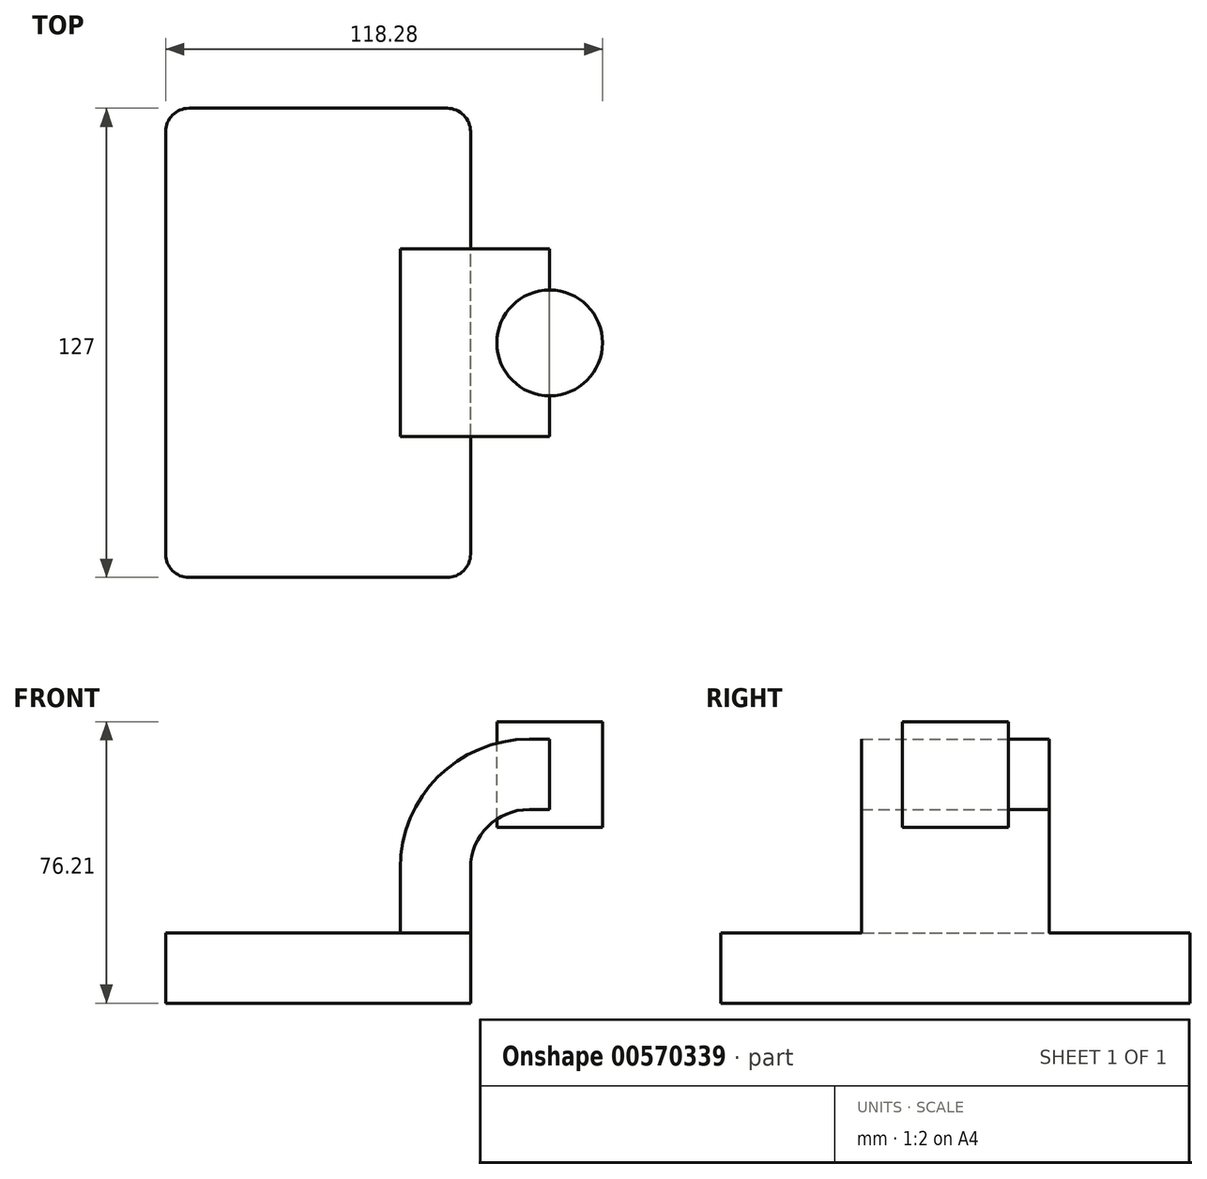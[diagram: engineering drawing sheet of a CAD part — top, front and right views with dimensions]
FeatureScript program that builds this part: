
annotation { "Feature Type Name" : "Feature", "Feature Type Description" : "" }
export const myFeature = defineFeature(function(context is Context, id is Id, definition is map)
    precondition{}
    {
        {
            var Q0;
            Q0=qCreatedBy(makeId("Front.planeOp"),FACE);
            var sketch = newSketch(context, id + "F0", { "sketchPlane" : qUnion([Q0])});
            skLineSegment(sketch, "E0.bottom", {"start": v(-41.28, 9.52) * mm, "end": v(41.27, 9.53) * mm});
            skLineSegment(sketch, "E0.top", {"start": v(-41.28, -9.53) * mm, "end": v(41.28, -9.53) * mm});
            skLineSegment(sketch, "E0.left", {"start": v(-41.28, 9.52) * mm, "end": v(-41.28, -9.53) * mm});
            skLineSegment(sketch, "E0.right", {"start": v(41.27, 9.53) * mm, "end": v(41.28, -9.52) * mm});
            skPoint(sketch, "E0.middle", {"position": v(0, 0) * mm});
            skLineSegment(sketch, "E1.bottom", {"start": v(62.7, 66.67) * mm, "end": v(113.5, 66.67) * mm});
            skLineSegment(sketch, "E1.top", {"start": v(62.7, 38.1) * mm, "end": v(113.5, 38.1) * mm});
            skLineSegment(sketch, "E1.left", {"start": v(62.7, 66.67) * mm, "end": v(62.7, 38.1) * mm});
            skLineSegment(sketch, "E1.right", {"start": v(113.5, 66.67) * mm, "end": v(113.5, 38.1) * mm});
            skPoint(sketch, "E1.middle", {"position": v(88.1, 52.39) * mm});
            skLineSegment(sketch, "E2", {"start": v(41.27, 9.53) * mm, "end": v(41.27, 27) * mm});
            skArc(sketch, "E3", {"start": v(41.27, 27) * mm, "mid": v(45.92, 38.23) * mm, "end": v(57.15, 42.88) * mm});
            skLineSegment(sketch, "E4", {"start": v(57.15, 42.88) * mm, "end": v(77, 42.88) * mm});
            skLineSegment(sketch, "E5.0", {"start": v(57.15, 61.93) * mm, "end": v(77, 61.93) * mm});
            skArc(sketch, "E5.1", {"start": v(22.22, 27) * mm, "mid": v(32.45, 51.7) * mm, "end": v(57.15, 61.93) * mm});
            skLineSegment(sketch, "E5.2", {"start": v(22.22, 9.53) * mm, "end": v(22.22, 27) * mm});
            skLineSegment(sketch, "E6", {"start": v(77.01, 38.1) * mm, "end": v(77.01, 66.67) * mm});
            skFitSpline(sketch, "E7", {"points": [v(-41.28, 9.52) * mm, v(57.15, 61.93) * mm], "startDerivative": vector(26.38, 101.36) * mm, "endDerivative": vector(135.16, -4.81) * mm});
            skSolve(sketch);
        }
        {
            var Q0;
            Q0=makeQuery(id+"F0.imprint","IMPRINT",FACE,{"disambiguationData":[TD([[makeQuery(id+"F0.imprint","IMPRINT",EDGE,{"derivedFrom":sQuery(id+"F0.wireOp",EDGE,"E0.top")}),1.0]])]});
            extrude(context, id + "F1", {"entities" : qUnion([Q0]), "endBound" : BoundingType.SYMMETRIC, "depth" : 127 * mm, "offsetDistance" : 25.4 * mm});
        }
        {
            var Q0;
            {var subQ1=sQuery(id+"F0.wireOp",EDGE,"E2");Q0=makeQuery(id+"F0.imprint","IMPRINT",FACE,{"disambiguationData":[TD([[makeQuery(id+"F0.imprint","IMPRINT",EDGE,{"derivedFrom":subQ1}),1.0]])]});}
            extrude(context, id + "F2", {"entities" : qUnion([Q0]), "operationType" : NewBodyOperationType.ADD, "endBound" : BoundingType.SYMMETRIC, "depth" : 50.8 * mm, "offsetDistance" : 25.4 * mm});
        }
        {
            var Q0;
            Q0=makeQuery(id+"F0.imprint","IMPRINT",FACE,{"disambiguationData":[TD([[makeQuery(id+"F0.imprint","IMPRINT",EDGE,{"derivedFrom":sQuery(id+"F0.wireOp",EDGE,"E5.1")}),1.0]])]});
            extrude(context, id + "F3", {"entities" : qUnion([Q0]), "operationType" : NewBodyOperationType.ADD, "endBound" : BoundingType.SYMMETRIC, "depth" : 15.88 * mm, "offsetDistance" : 25.4 * mm});
        }
        {
            var Q0;
            {var subQ6=sQuery(id+"F0.wireOp",EDGE,"E6");Q0=makeQuery(id+"F0.imprint","IMPRINT",FACE,{"disambiguationData":[TD([[makeQuery(id+"F0.imprint","IMPRINT",EDGE,{"derivedFrom":subQ6}),1.0]])]});}
            var Q1;
            Q1=sQuery(id+"F0.wireOp",EDGE,"E1.left");
            revolve(context, id + "F4", {"entities" : qUnion([Q0]), "axis" : qUnion([Q1]), "revolveType" : RevolveType.FULL});
        }
        {
            var Q0;
            Q0=makeQuery(id+"F1.opExtrude","CAP_EDGE",EDGE,{"disambiguationData":[OSD([sQuery(id+"F0.wireOp",EDGE,"E0.left")])],"isStart":false});
            var Q1;
            Q1=makeQuery(id+"F1.opExtrude","CAP_EDGE",EDGE,{"disambiguationData":[OSD([sQuery(id+"F0.wireOp",EDGE,"E0.right")])],"isStart":false});
            var Q2;
            Q2=makeQuery(id+"F1.opExtrude","CAP_EDGE",EDGE,{"disambiguationData":[OSD([sQuery(id+"F0.wireOp",EDGE,"E0.right")])],"isStart":true});
            var Q3;
            Q3=makeQuery(id+"F1.opExtrude","CAP_EDGE",EDGE,{"disambiguationData":[OSD([sQuery(id+"F0.wireOp",EDGE,"E0.left")])],"isStart":true});
            fillet(context, id + "F5", {"entities" : qUnion([Q0, Q1, Q2, Q3]), "radius" : 6.35 * mm, "tangentPropagation" : true, "allowEdgeOverflow" : false});
        }
    });
